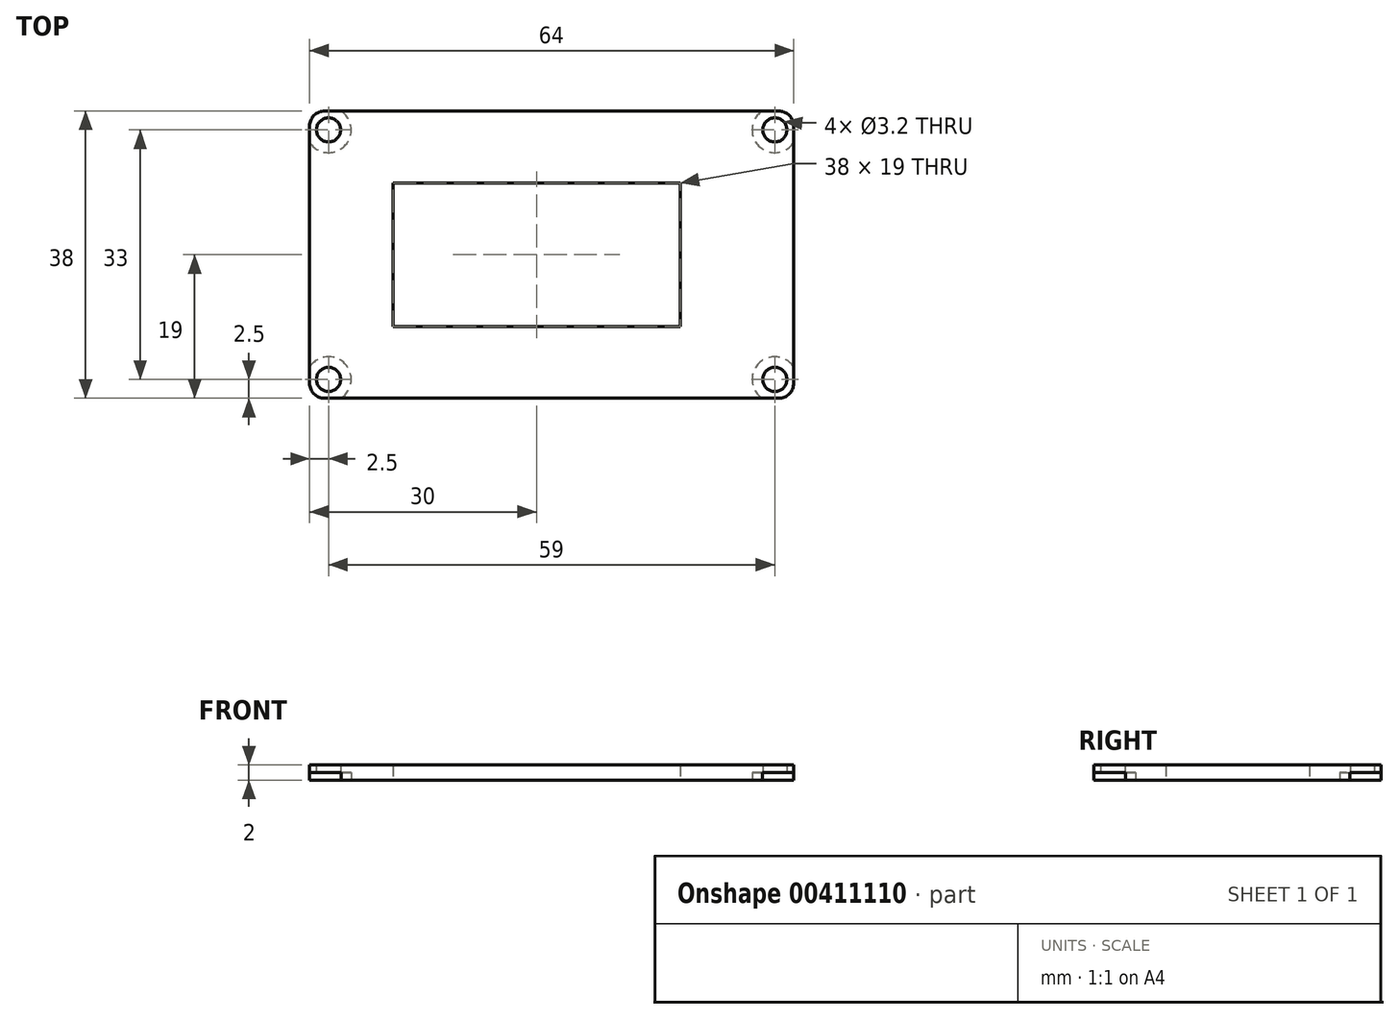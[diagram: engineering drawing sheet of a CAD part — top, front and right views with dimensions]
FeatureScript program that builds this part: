
annotation { "Feature Type Name" : "Feature", "Feature Type Description" : "" }
export const myFeature = defineFeature(function(context is Context, id is Id, definition is map)
    precondition{}
    {
        {
            var Q0;
            Q0=qCreatedBy(makeId("Top.planeOp"),FACE);
            var sketch = newSketch(context, id + "F0", { "sketchPlane" : qUnion([Q0])});
            skLineSegment(sketch, "E0.bottom", {"start": v(0, 0) * mm, "end": v(64, 0) * mm});
            skLineSegment(sketch, "E0.top", {"start": v(0, 38) * mm, "end": v(64, 38) * mm});
            skLineSegment(sketch, "E0.left", {"start": v(0, 0) * mm, "end": v(0, 38) * mm});
            skLineSegment(sketch, "E0.right", {"start": v(64, 0) * mm, "end": v(64, 38) * mm});
            skLineSegment(sketch, "E1.bottom", {"start": v(11, 9.5) * mm, "end": v(49, 9.5) * mm});
            skLineSegment(sketch, "E1.top", {"start": v(11, 28.5) * mm, "end": v(49, 28.5) * mm});
            skLineSegment(sketch, "E1.left", {"start": v(11, 9.5) * mm, "end": v(11, 28.5) * mm});
            skLineSegment(sketch, "E1.right", {"start": v(49, 9.5) * mm, "end": v(49, 28.5) * mm});
            skPoint(sketch, "E2", {"position": v(0, 19) * mm});
            skPoint(sketch, "E3", {"position": v(11, 19) * mm});
            skPoint(sketch, "E4", {"position": v(30, 28.5) * mm});
            skPoint(sketch, "E5", {"position": v(32, 38) * mm});
            skSolve(sketch);
        }
        {
            var Q0;
            Q0=makeQuery(id+"F0.imprint","IMPRINT",FACE,{"disambiguationData":[TD([[makeQuery(id+"F0.imprint","IMPRINT",EDGE,{"derivedFrom":sQuery(id+"F0.wireOp",EDGE,"E0.bottom")}),1.0]])]});
            extrude(context, id + "F1", {"entities" : qUnion([Q0]), "depth" : 2 * mm});
        }
        {
            var Q0;
            Q0=makeQuery(id+"F1.opExtrude","SWEPT_EDGE",EDGE,{"disambiguationData":[OSD([sQuery(id+"F0.wireOp",EDGE,"E0.top"),sQuery(id+"F0.wireOp",EDGE,"E0.left")])]});
            var Q1;
            Q1=makeQuery(id+"F1.opExtrude","SWEPT_EDGE",EDGE,{"disambiguationData":[OSD([sQuery(id+"F0.wireOp",EDGE,"E0.bottom"),sQuery(id+"F0.wireOp",EDGE,"E0.left")])]});
            var Q2;
            Q2=makeQuery(id+"F1.opExtrude","SWEPT_EDGE",EDGE,{"disambiguationData":[OSD([sQuery(id+"F0.wireOp",EDGE,"E0.bottom"),sQuery(id+"F0.wireOp",EDGE,"E0.right")])]});
            var Q3;
            Q3=makeQuery(id+"F1.opExtrude","SWEPT_EDGE",EDGE,{"disambiguationData":[OSD([sQuery(id+"F0.wireOp",EDGE,"E0.top"),sQuery(id+"F0.wireOp",EDGE,"E0.right")])]});
            fillet(context, id + "F2", {"entities" : qUnion([Q0, Q1, Q2, Q3]), "radius" : 2 * mm, "tangentPropagation" : true, "allowEdgeOverflow" : false});
        }
        {
            var Q0;
            Q0=makeQuery(id+"F1.opExtrude","CAP_FACE",FACE,{"disambiguationData":[OSD([sQuery(id+"F0.wireOp",EDGE,"E0.bottom"),sQuery(id+"F0.wireOp",EDGE,"E0.top"),sQuery(id+"F0.wireOp",EDGE,"E0.left"),sQuery(id+"F0.wireOp",EDGE,"E0.right"),sQuery(id+"F0.wireOp",EDGE,"E1.bottom"),sQuery(id+"F0.wireOp",EDGE,"E1.top"),sQuery(id+"F0.wireOp",EDGE,"E1.left"),sQuery(id+"F0.wireOp",EDGE,"E1.right")])],"isStart":true});
            var sketch = newSketch(context, id + "F3", { "sketchPlane" : qUnion([Q0])});
            skLineSegment(sketch, "E6.bottom", {"start": v(2.5, -2.5) * mm, "end": v(61.5, -2.5) * mm, "construction": true});
            skLineSegment(sketch, "E6.top", {"start": v(2.5, -35.5) * mm, "end": v(61.5, -35.5) * mm, "construction": true});
            skLineSegment(sketch, "E6.left", {"start": v(2.5, -2.5) * mm, "end": v(2.5, -35.5) * mm, "construction": true});
            skLineSegment(sketch, "E6.right", {"start": v(61.5, -2.5) * mm, "end": v(61.5, -35.5) * mm, "construction": true});
            skSolve(sketch);
        }
        {
            var Q0;
            Q0=sQuery(id+"F3.wireOp",VERTEX,"E6.bottom.start");
            var Q1;
            Q1=sQuery(id+"F3.wireOp",VERTEX,"E6.left.end");
            var Q2;
            Q2=sQuery(id+"F3.wireOp",VERTEX,"E6.right.end");
            var Q3;
            Q3=sQuery(id+"F3.wireOp",VERTEX,"E6.right.start");
            var Q4;
            Q4=makeQuery(id+"F1.opExtrude","SWEPT_BODY",BODY,{"disambiguationData":[OSD([sQuery(id+"F0.wireOp",EDGE,"E0.bottom"),sQuery(id+"F0.wireOp",EDGE,"E0.top"),sQuery(id+"F0.wireOp",EDGE,"E0.left"),sQuery(id+"F0.wireOp",EDGE,"E0.right"),sQuery(id+"F0.wireOp",EDGE,"E1.bottom"),sQuery(id+"F0.wireOp",EDGE,"E1.top"),sQuery(id+"F0.wireOp",EDGE,"E1.left"),sQuery(id+"F0.wireOp",EDGE,"E1.right")])]});
            hole(context, id + "F4", {"style" : HoleStyle.C_BORE, "endStyle" : HoleEndStyle.THROUGH, "holeDiameter" : 3.2 * mm, "cBoreDiameter" : 6 * mm, "cBoreDepth" : 1 * mm, "isTappedThrough" : true, "tappedDepth" : 12 * mm, "tapClearance" : 3, "locations" : qUnion([Q0, Q1, Q2, Q3]), "scope" : qUnion([Q4])});
        }
    });
